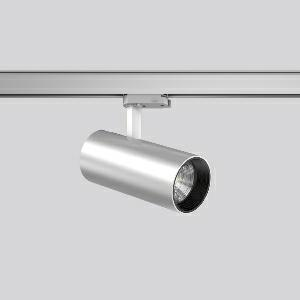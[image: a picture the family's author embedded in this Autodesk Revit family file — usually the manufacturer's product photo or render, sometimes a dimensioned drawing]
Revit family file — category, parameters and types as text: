
# Revit family: deecos_s_mini_742199_004_76_0967
name_source: partatom
category: Lighting Fixtures
units: mm (PartAtom-declared; Revit-internal decimal feet)

## family parameters
Cut with Voids When Loaded = No
Host = Face
Light Source = No
Part Type = Normal
Room Calculation Point = No
Round Connector Dimension = Use Diameter
Shared = No

## types (1)
- DEECOS S mini (1 x LED Modul 930, 2100 lm, 3000)
    Apparent Load = 20 VA
    Approval mark = CE
    CIE Flux Codes = 96 100 100 100 100
    Color Rendering = 90
    Color Temperature = 3000
    Default Elevation = 1800 mm
    Description = Series: DEECOS S mini
LED surface-mounted projector in modern design with no visible cooling ribs. Housing: die-cast aluminium, powder-coated. Rotation range: 356°. Swivel range: 90°. Black plastic ring and recessed LED to prevent glare from the side. Optical assembly with lens made of plastic (polycarbonate) for the best homogeneous light distribution - can be changed without tools. Best colour rendering index Ra>90. With adapter for RZB 3-circuit DALI tracks. Suitable for Track on ceiling, Wall track. High quality converter without flickering and stroboscopic effect. The following accessories can be mounted without use of tools: interchangeable lenses, decorative glasses, honeycomb louvre, clear and frosted diffusers, white interchangeable plastic ring. 
Colour: silver
Diameter: 87 mm
Height: 214 mm
Lamp: LED
Socket: without socket
Colour temperature: 3000K
Colour rendering index (CRI): 92
System power: 20 W
Rated luminous flux: 2100 lm
Luminous efficiency: 105 lm/W
Control gear: Converter, dimmable, DALI
Protection class: I
Type of protection: IP 20
    Height = 214 mm
    Lamp = 1 x LED Modul 930
    Lamp Light Flux = 2100 lm
    Lamp count = 1
    Length = 87 mm
    Lifetime = 50000 h
    Luminous efficacy = 105 lm/W
    Manufacturer = RZB
    ModVariant = No
    Model = 742199.004.76
    Mounting Place = Ceiling
    Mounting Type = Rail mounted
    Number of Poles = 1
    OnlyDefault = Yes
    Power Factor = 1
    Product Name = DEECOS S mini
    Product group = Track mounted projectors
    ProductGroupID = 301
    Protection Class = Protection class I
    Protection Degree = IP 20
    RLX_Detail_Level = 1
    RLX_Emergency_Light_Flux = 0 lm
    RLX_Emergency_Type = 0
    RLX_Emergency_Type_DB = No
    RlxData = <blob elided: 37473 chars, md5=1a967f5b>
    Socket = socket
    Standby Power = 0 W
    System Light Flux = 2100 lm
    System Power = 20 W
    Type Comments = Product without accessories
    Type Image = 741930.004.jpg
    URL = http://relux.com
    VarID = ---
    Voltage = 230 V
    Voltage Range = 220-240 V
    Weight = 0.00 kg
    Width = 0 mm  [stored 0 ft]

note: [stored X ft] marks values corroborated as IEEE doubles in the binary element streams (Revit-internal decimal feet)

## geometry (parser evidence)
native form markers: Blend x4, Sweep x12
no freeform markers — native parametric forms only
